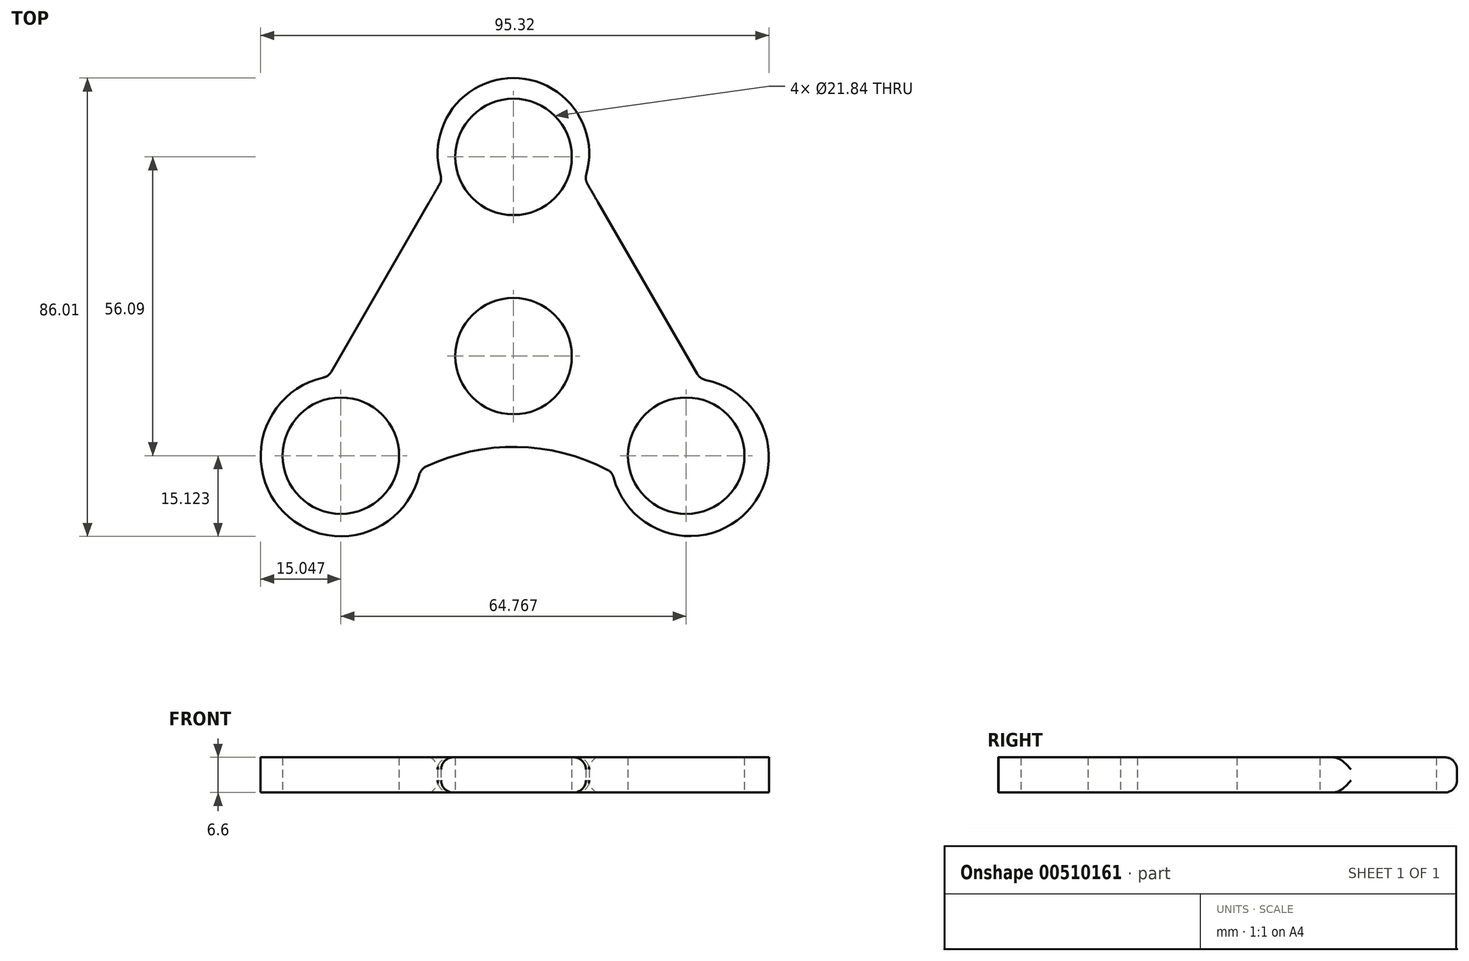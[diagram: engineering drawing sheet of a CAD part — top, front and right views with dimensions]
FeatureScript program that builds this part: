
annotation { "Feature Type Name" : "Feature", "Feature Type Description" : "" }
export const myFeature = defineFeature(function(context is Context, id is Id, definition is map)
    precondition{}
    {
        {
            var Q0;
            Q0=qCreatedBy(makeId("Top.planeOp"),FACE);
            var sketch = newSketch(context, id + "F0", { "sketchPlane" : qUnion([Q0])});
            skCircle(sketch, "E0", {"center": v(0, 0) * mm, "radius": 10.92 * mm});
            skLineSegment(sketch, "E1", {"start": v(0, 0) * mm, "end": v(0, 37.4) * mm, "construction": true});
            skCircle(sketch, "E2", {"center": v(0, 37.4) * mm, "radius": 10.92 * mm});
            skLineSegment(sketch, "E3", {"start": v(10.92, 37.4) * mm, "end": v(-10.92, 37.4) * mm, "construction": true});
            skArc(sketch, "E4.1.1", {"start": v(-42.6, -49.64) * mm, "mid": v(-42.43, -49.54) * mm, "end": v(-42.27, -49.44) * mm});
            skArc(sketch, "E4.2.1", {"start": v(35.81, -51.1) * mm, "mid": v(36.72, -51.84) * mm, "end": v(37.7, -52.47) * mm});
            skPoint(sketch, "E4.center", {"position": v(-1.64, -15.27) * mm});
            skLineSegment(sketch, "E5", {"start": v(-53.52, -30.72) * mm, "end": v(-53.52, -30.72) * mm});
            skPoint(sketch, "E6.center", {"position": v(-2.33, -14.15) * mm});
            skArc(sketch, "E7.trimOffspring", {"start": v(-42.27, -49.44) * mm, "mid": v(-42.43, -49.54) * mm, "end": v(-42.6, -49.64) * mm});
            skLineSegment(sketch, "E8.trimOffspring", {"start": v(-10.92, 37.4) * mm, "end": v(-10.92, 37.4) * mm});
            skArc(sketch, "E9.trimOffspring", {"start": v(48.28, -33.37) * mm, "mid": v(48.45, -33.46) * mm, "end": v(48.61, -33.56) * mm});
            skArc(sketch, "E10.trimOffspring", {"start": v(48.61, -33.56) * mm, "mid": v(48.45, -33.46) * mm, "end": v(48.28, -33.37) * mm});
            skCircle(sketch, "E11.1.0", {"center": v(-32.38, -18.7) * mm, "radius": 10.92 * mm});
            skCircle(sketch, "E11.2.0", {"center": v(32.38, -18.7) * mm, "radius": 10.92 * mm});
            skPoint(sketch, "E11.center", {"position": v(0.26, 1.12) * mm});
            skLineSegment(sketch, "E12", {"start": v(-11.64, 23.03) * mm, "end": v(-11.37, 22.61) * mm});
            skLineSegment(sketch, "E13.1.0", {"start": v(-37.84, -9.24) * mm, "end": v(-26.92, -28.16) * mm, "construction": true});
            skLineSegment(sketch, "E13.2.0", {"start": v(26.92, -28.16) * mm, "end": v(37.84, -9.24) * mm, "construction": true});
            skLineSegment(sketch, "E14", {"start": v(-34.73, -3.85) * mm, "end": v(-13.39, 33.12) * mm});
            skLineSegment(sketch, "E15", {"start": v(13.35, 33.18) * mm, "end": v(35, -4.3) * mm});
            skArc(sketch, "E16", {"start": v(18.55, -21.85) * mm, "mid": v(0.6, -17.05) * mm, "end": v(-17.48, -21.28) * mm});
            skLineSegment(sketch, "E17", {"start": v(23.64, -25.25) * mm, "end": v(23.72, -25.35) * mm});
            skArc(sketch, "E18", {"start": v(-34.73, -3.85) * mm, "mid": v(-43.07, -29.35) * mm, "end": v(-17.48, -21.28) * mm});
            skArc(sketch, "E19", {"start": v(18.55, -21.85) * mm, "mid": v(43.89, -29.1) * mm, "end": v(35, -4.3) * mm});
            skArc(sketch, "E20", {"start": v(13.35, 33.18) * mm, "mid": v(-0.06, 52.2) * mm, "end": v(-13.39, 33.12) * mm});
            skSolve(sketch);
        }
        {
            var Q0;
            Q0=makeQuery(id+"F0.imprint","IMPRINT",FACE,{"disambiguationData":[TD([[makeQuery(id+"F0.imprint","IMPRINT",EDGE,{"derivedFrom":sQuery(id+"F0.wireOp",EDGE,"E0")}),-1.0]])]});
            extrude(context, id + "F1", {"entities" : qUnion([Q0]), "depth" : 6.6 * mm, "offsetDistance" : 25.4 * mm});
        }
        {
            var Q0;
            Q0=makeQuery(id+"F1.opExtrude","SWEPT_EDGE",EDGE,{"disambiguationData":[OSD([sQuery(id+"F0.wireOp",EDGE,"E16"),sQuery(id+"F0.wireOp",EDGE,"E18")])]});
            var Q1;
            Q1=makeQuery(id+"F1.opExtrude","SWEPT_EDGE",EDGE,{"disambiguationData":[OSD([sQuery(id+"F0.wireOp",EDGE,"E16"),sQuery(id+"F0.wireOp",EDGE,"E19")])]});
            var Q2;
            Q2=makeQuery(id+"F1.opExtrude","SWEPT_EDGE",EDGE,{"disambiguationData":[OSD([sQuery(id+"F0.wireOp",EDGE,"E15"),sQuery(id+"F0.wireOp",EDGE,"E19")])]});
            var Q3;
            Q3=makeQuery(id+"F1.opExtrude","SWEPT_EDGE",EDGE,{"disambiguationData":[OSD([sQuery(id+"F0.wireOp",EDGE,"E14"),sQuery(id+"F0.wireOp",EDGE,"E20")])]});
            var Q4;
            Q4=makeQuery(id+"F1.opExtrude","SWEPT_EDGE",EDGE,{"disambiguationData":[OSD([sQuery(id+"F0.wireOp",EDGE,"E14"),sQuery(id+"F0.wireOp",EDGE,"E18")])]});
            var Q5;
            Q5=makeQuery(id+"F1.opExtrude","SWEPT_EDGE",EDGE,{"disambiguationData":[OSD([sQuery(id+"F0.wireOp",EDGE,"E15"),sQuery(id+"F0.wireOp",EDGE,"E20")])]});
            var Q6;
            Q6=makeQuery(id+"F1.opExtrude","CAP_EDGE",EDGE,{"disambiguationData":[OSD([sQuery(id+"F0.wireOp",EDGE,"E20")])],"isStart":true});
            var Q7;
            Q7=makeQuery(id+"F1.opExtrude","CAP_EDGE",EDGE,{"disambiguationData":[OSD([sQuery(id+"F0.wireOp",EDGE,"E20")])],"isStart":false});
            fillet(context, id + "F2", {"entities" : qUnion([Q0, Q1, Q2, Q3, Q4, Q5, Q6, Q7]), "radius" : 2.3 * mm, "tangentPropagation" : true, "allowEdgeOverflow" : false});
        }
    });
